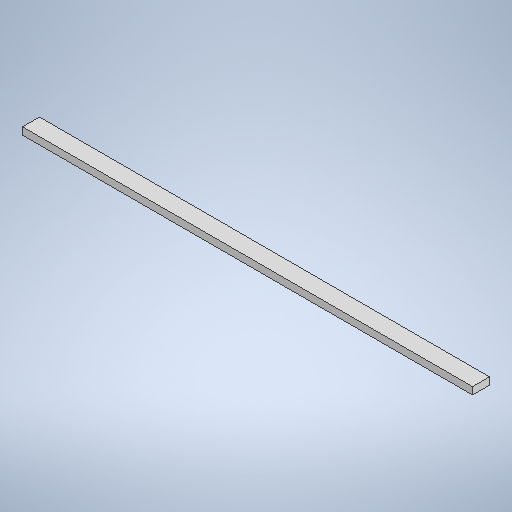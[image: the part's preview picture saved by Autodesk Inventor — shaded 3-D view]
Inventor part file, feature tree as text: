
AUTODESK INVENTOR PART (.ipt)
format: ipt  version: 2025 (Build 290162000, 162)  size: 248,320 bytes
history: native  units: in
note: dims shown in document units (in); Inventor stores cm internally (conversion verified against a paired STEP export)
features: extrude x1, sketch x1
ambient origin geometry x8: Origin, YZ Plane, XZ Plane, XY Plane, X Axis, Y Axis, Z Axis, Center Point
bodies: Solid1 (feature_tree)
feature tree (2):
  extrude  "Extrusion1"  Depth=3.5in
  sketch  "Sketch1"  dims[d0=93.0in d1=3.5in d2=1.5in d3=0.0in]
